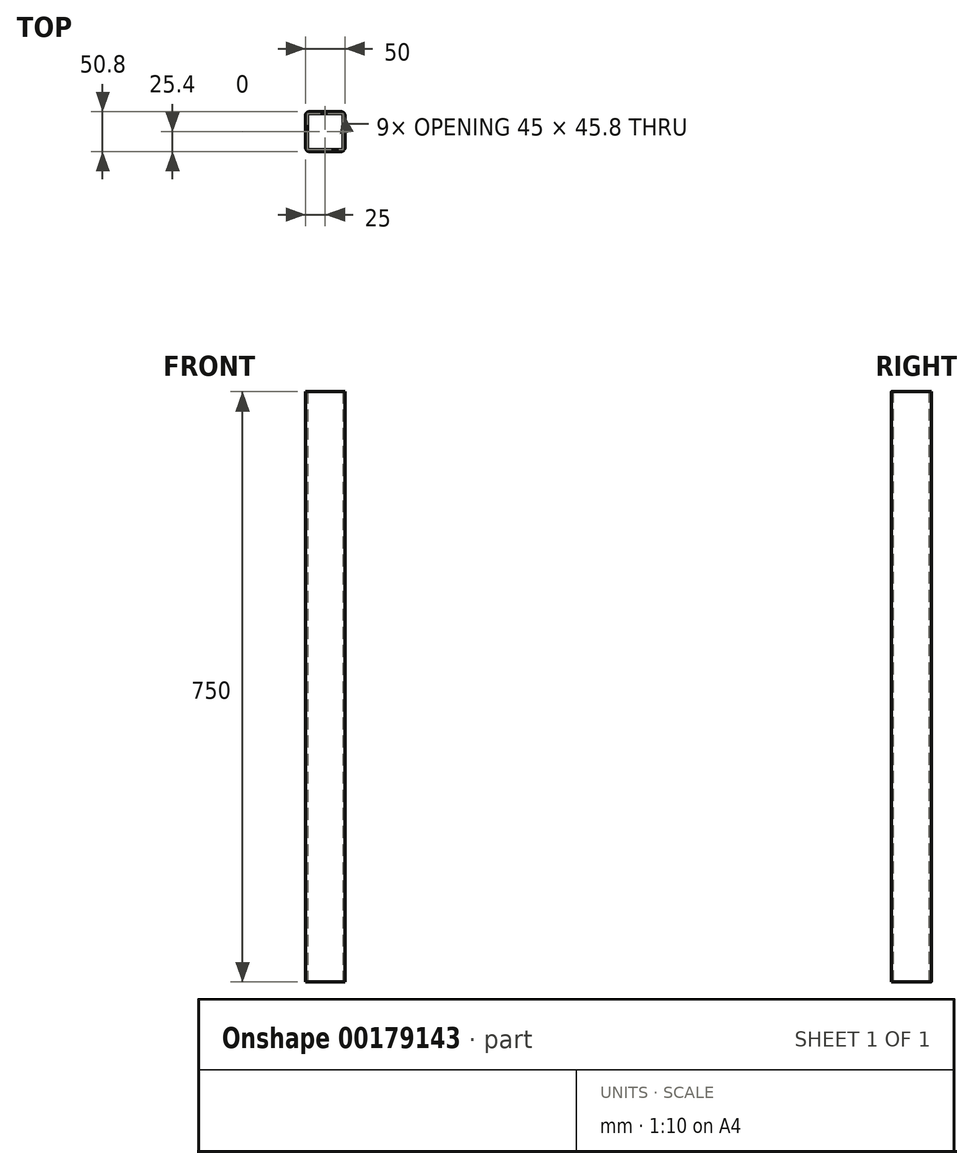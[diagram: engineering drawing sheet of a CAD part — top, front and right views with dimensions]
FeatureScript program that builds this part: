
annotation { "Feature Type Name" : "Feature", "Feature Type Description" : "" }
export const myFeature = defineFeature(function(context is Context, id is Id, definition is map)
    precondition{}
    {
        {
            var Q0;
            Q0=qCreatedBy(makeId("Top.planeOp"),FACE);
            var sketch = newSketch(context, id + "F0", { "sketchPlane" : qUnion([Q0])});
            skLineSegment(sketch, "E0.bottom", {"start": v(-25, 25) * mm, "end": v(25, 25) * mm});
            skLineSegment(sketch, "E0.top", {"start": v(-25, -25.8) * mm, "end": v(25, -25.8) * mm});
            skLineSegment(sketch, "E0.left", {"start": v(-25, 25) * mm, "end": v(-25, -25.8) * mm});
            skLineSegment(sketch, "E0.right", {"start": v(25, 25) * mm, "end": v(25, -25.8) * mm});
            skSolve(sketch);
        }
        {
            var Q0;
            Q0 = qSketchRegion(id + "F0", true);
            extrude(context, id + "F1", {"entities" : qUnion([Q0]), "depth" : 750 * mm});
        }
        {
            var Q0;
            Q0=makeQuery(id+"F1.opExtrude","SWEPT_EDGE",EDGE,{"disambiguationData":[OSD([sQuery(id+"F0.wireOp",EDGE,"E0.bottom"),sQuery(id+"F0.wireOp",EDGE,"E0.right")])]});
            var Q1;
            Q1=makeQuery(id+"F1.opExtrude","SWEPT_EDGE",EDGE,{"disambiguationData":[OSD([sQuery(id+"F0.wireOp",EDGE,"E0.top"),sQuery(id+"F0.wireOp",EDGE,"E0.right")])]});
            var Q2;
            Q2=makeQuery(id+"F1.opExtrude","SWEPT_EDGE",EDGE,{"disambiguationData":[OSD([sQuery(id+"F0.wireOp",EDGE,"E0.bottom"),sQuery(id+"F0.wireOp",EDGE,"E0.left")])]});
            var Q3;
            Q3=makeQuery(id+"F1.opExtrude","SWEPT_EDGE",EDGE,{"disambiguationData":[OSD([sQuery(id+"F0.wireOp",EDGE,"E0.top"),sQuery(id+"F0.wireOp",EDGE,"E0.left")])]});
            fillet(context, id + "F2", {"entities" : qUnion([Q0, Q1, Q2, Q3]), "radius" : 5 * mm, "tangentPropagation" : true, "allowEdgeOverflow" : false});
        }
        {
            var Q0;
            Q0=makeQuery(id+"F1.opExtrude","CAP_FACE",FACE,{"disambiguationData":[OSD([sQuery(id+"F0.wireOp",EDGE,"E0.bottom"),sQuery(id+"F0.wireOp",EDGE,"E0.top"),sQuery(id+"F0.wireOp",EDGE,"E0.left"),sQuery(id+"F0.wireOp",EDGE,"E0.right")])],"isStart":false});
            var Q1;
            Q1=makeQuery(id+"F1.opExtrude","CAP_FACE",FACE,{"disambiguationData":[OSD([sQuery(id+"F0.wireOp",EDGE,"E0.bottom"),sQuery(id+"F0.wireOp",EDGE,"E0.top"),sQuery(id+"F0.wireOp",EDGE,"E0.left"),sQuery(id+"F0.wireOp",EDGE,"E0.right")])],"isStart":true});
            shell(context, id + "F3", {"entities" : qUnion([Q0, Q1]), "thickness" : 2.5 * mm});
        }
    });
